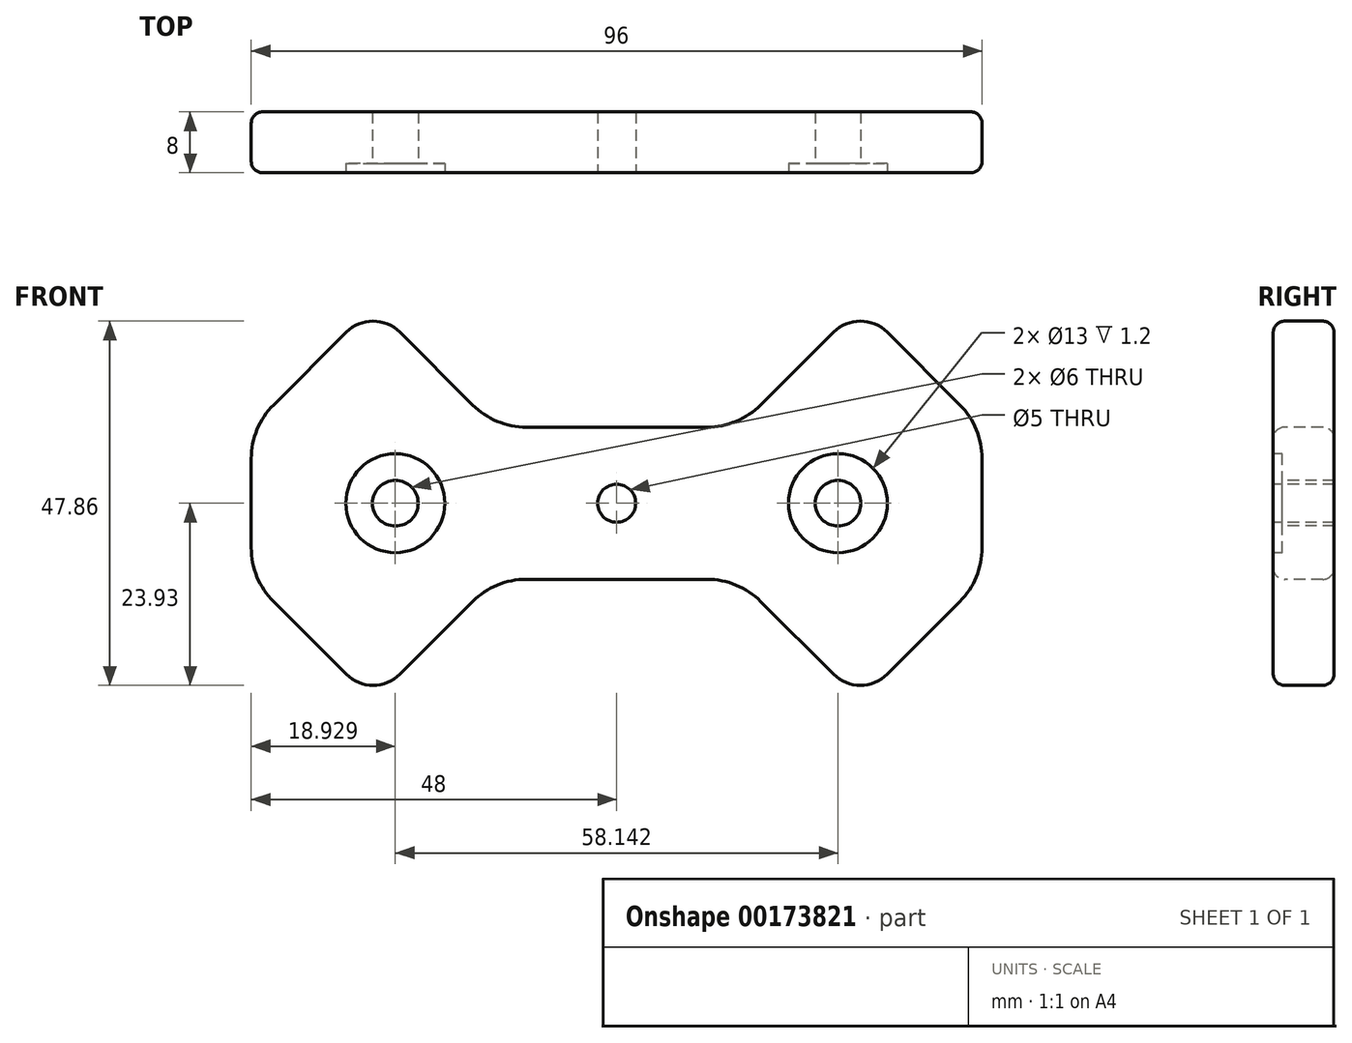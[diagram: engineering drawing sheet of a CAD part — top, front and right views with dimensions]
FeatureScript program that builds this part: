
annotation { "Feature Type Name" : "Feature", "Feature Type Description" : "" }
export const myFeature = defineFeature(function(context is Context, id is Id, definition is map)
    precondition{}
    {
        {
            var Q0;
            Q0=qCreatedBy(makeId("Front.planeOp"),FACE);
            var sketch = newSketch(context, id + "F0", { "sketchPlane" : qUnion([Q0])});
            skLineSegment(sketch, "E0", {"start": v(22, 90.61) * mm, "end": v(22, -125.4) * mm, "construction": true});
            skLineSegment(sketch, "E1", {"start": v(25.54, 3.54) * mm, "end": v(146.18, 124.18) * mm, "construction": true});
            skLineSegment(sketch, "E2", {"start": v(25.54, -3.54) * mm, "end": v(137.79, -115.79) * mm, "construction": true});
            skPoint(sketch, "E3.visualSharp", {"position": v(22, 0) * mm});
            skArc(sketch, "E3.filletArc", {"start": v(25.54, 3.54) * mm, "mid": v(24.07, 0) * mm, "end": v(25.54, -3.54) * mm, "construction": true});
            skLineSegment(sketch, "E4.0", {"start": v(24.2, 4.88) * mm, "end": v(144.83, 125.52) * mm});
            skArc(sketch, "E4.1", {"start": v(24.2, 4.88) * mm, "mid": v(22.17, 0) * mm, "end": v(24.2, -4.88) * mm});
            skLineSegment(sketch, "E4.2", {"start": v(24.2, -4.88) * mm, "end": v(136.44, -117.13) * mm});
            skLineSegment(sketch, "E5.0", {"start": v(26.88, 2.2) * mm, "end": v(147.52, 122.83) * mm});
            skArc(sketch, "E5.1", {"start": v(26.88, 2.2) * mm, "mid": v(25.97, 0) * mm, "end": v(26.88, -2.2) * mm});
            skLineSegment(sketch, "E5.2", {"start": v(26.88, -2.2) * mm, "end": v(139.13, -114.44) * mm});
            skLineSegment(sketch, "E6", {"start": v(0, 0) * mm, "end": v(0, 10) * mm});
            skLineSegment(sketch, "E7", {"start": v(0, 10) * mm, "end": v(11.86, 10) * mm});
            skLineSegment(sketch, "E8", {"start": v(48, 5.86) * mm, "end": v(48, -5.86) * mm});
            skLineSegment(sketch, "E9", {"start": v(0, -10) * mm, "end": v(0, 0) * mm});
            skLineSegment(sketch, "E10", {"start": v(45.07, 12.93) * mm, "end": v(35.54, 22.46) * mm});
            skLineSegment(sketch, "E11", {"start": v(28.46, 22.46) * mm, "end": v(18.93, 12.93) * mm});
            skLineSegment(sketch, "E12", {"start": v(18.93, -12.93) * mm, "end": v(28.46, -22.46) * mm});
            skLineSegment(sketch, "E13", {"start": v(35.54, -22.46) * mm, "end": v(45.07, -12.93) * mm});
            skLineSegment(sketch, "E14.trimOffspring", {"start": v(11.86, -10) * mm, "end": v(0, -10) * mm});
            skCircle(sketch, "E15", {"center": v(29.07, 0) * mm, "radius": 6.5 * mm});
            skPoint(sketch, "E16.visualSharp", {"position": v(16, 10) * mm});
            skArc(sketch, "E16.filletArc", {"start": v(11.86, 10) * mm, "mid": v(15.68, 10.76) * mm, "end": v(18.93, 12.93) * mm});
            skPoint(sketch, "E17.visualSharp", {"position": v(16, -10) * mm});
            skArc(sketch, "E17.filletArc", {"start": v(18.93, -12.93) * mm, "mid": v(15.68, -10.76) * mm, "end": v(11.86, -10) * mm});
            skPoint(sketch, "E18.visualSharp", {"position": v(32, 26) * mm});
            skArc(sketch, "E18.filletArc", {"start": v(35.54, 22.46) * mm, "mid": v(32, 23.93) * mm, "end": v(28.46, 22.46) * mm});
            skPoint(sketch, "E19.visualSharp", {"position": v(32, -26) * mm});
            skArc(sketch, "E19.filletArc", {"start": v(28.46, -22.46) * mm, "mid": v(32, -23.93) * mm, "end": v(35.54, -22.46) * mm});
            skPoint(sketch, "E20.visualSharp", {"position": v(48, 10) * mm});
            skArc(sketch, "E20.filletArc", {"start": v(48, 5.86) * mm, "mid": v(47.24, 9.68) * mm, "end": v(45.07, 12.93) * mm});
            skPoint(sketch, "E21.visualSharp", {"position": v(48, -10) * mm});
            skArc(sketch, "E21.filletArc", {"start": v(45.07, -12.93) * mm, "mid": v(47.24, -9.68) * mm, "end": v(48, -5.86) * mm});
            skSolve(sketch);
        }
        {
            var Q0;
            Q0=qSketchRegion(id+"F0",true);
            var Q1;
            {var subQ0=sQuery(id+"F0.wireOp",EDGE,"E5.1");Q1=makeQuery(id+"F0.imprint","IMPRINT",FACE,{"disambiguationData":[TD([[makeQuery(id+"F0.imprint","IMPRINT",EDGE,{"derivedFrom":subQ0}),1.0]])]});}
            var Q2;
            {var subQ0=sQuery(id+"F0.wireOp",EDGE,"E5.1");Q2=makeQuery(id+"F0.imprint","IMPRINT",FACE,{"disambiguationData":[TD([[makeQuery(id+"F0.imprint","IMPRINT",EDGE,{"derivedFrom":subQ0}),-1.0]])]});}
            extrude(context, id + "F1", {"entities" : qUnion([Q0, Q1, Q2]), "oppositeDirection" : true, "depth" : 8 * mm, "offsetDistance" : 25 * mm});
        }
        {
            var Q0;
            Q0=makeQuery(id+"F1.opExtrude","SWEPT_FACE",FACE,{"disambiguationData":[OSD([sQuery(id+"F0.wireOp",EDGE,"E10")])]});
            var sketch = newSketch(context, id + "F2", { "sketchPlane" : qUnion([Q0])});
            skPoint(sketch, "E22.0", {"position": v(13.66, 0) * mm});
            skPoint(sketch, "E23.0", {"position": v(17.46, 0) * mm});
            skLineSegment(sketch, "E24", {"start": v(17.46, 0) * mm, "end": v(17.46, 1.1) * mm});
            skArc(sketch, "E25", {"start": v(17.46, 1.1) * mm, "mid": v(15.56, 3) * mm, "end": v(13.66, 1.1) * mm});
            skLineSegment(sketch, "E26", {"start": v(17.46, 0) * mm, "end": v(13.66, 0) * mm});
            skLineSegment(sketch, "E27", {"start": v(13.66, 0) * mm, "end": v(13.66, 1.1) * mm});
            skSolve(sketch);
        }
        {
            var Q0;
            Q0=makeQuery(id+"F2.imprint","IMPRINT",FACE,{"disambiguationData":[TD([[makeQuery(id+"F2.imprint","IMPRINT",EDGE,{"derivedFrom":sQuery(id+"F2.wireOp",EDGE,"E24")}),1.0]])]});
            var Q1;
            Q1=sQuery(id+"F0.wireOp",EDGE,"E4.0");
            var Q2;
            Q2=sQuery(id+"F0.wireOp",EDGE,"E4.1");
            var Q3;
            Q3=sQuery(id+"F0.wireOp",EDGE,"E4.2");
            sweep(context, id + "F3", {"operationType" : NewBodyOperationType.REMOVE, "profiles" : qUnion([Q0]), "path" : qUnion([Q1, Q2, Q3])});
        }
        {
            var Q0;
            {var subQ0=sQuery(id+"F0.wireOp",EDGE,"E5.1");Q0=makeQuery(id+"F0.imprint","IMPRINT",FACE,{"disambiguationData":[TD([[makeQuery(id+"F0.imprint","IMPRINT",EDGE,{"derivedFrom":subQ0}),1.0]])]});}
            var sketch = newSketch(context, id + "F4", { "sketchPlane" : qUnion([Q0])});
            skCircle(sketch, "E28.0", {"center": v(29.07, 0) * mm, "radius": 6.5 * mm});
            skSolve(sketch);
        }
        {
            var Q0;
            Q0=qSketchRegion(id+"F4",true);
            extrude(context, id + "F5", {"entities" : qUnion([Q0]), "operationType" : NewBodyOperationType.REMOVE, "oppositeDirection" : true, "depth" : 1.2 * mm, "offsetDistance" : 25 * mm});
        }
        {
            var Q0;
            {var subQ0=sQuery(id+"F0.wireOp",EDGE,"E5.1");Q0=makeQuery(id+"F0.imprint","IMPRINT",FACE,{"disambiguationData":[TD([[makeQuery(id+"F0.imprint","IMPRINT",EDGE,{"derivedFrom":subQ0}),1.0]])]});}
            var sketch = newSketch(context, id + "F6", { "sketchPlane" : qUnion([Q0])});
            skPoint(sketch, "E29.0", {"position": v(29.07, 0) * mm});
            skCircle(sketch, "E30", {"center": v(29.07, 0) * mm, "radius": 3 * mm});
            skSolve(sketch);
        }
        {
            var Q0;
            Q0=qSketchRegion(id+"F6",true);
            extrude(context, id + "F7", {"entities" : qUnion([Q0]), "operationType" : NewBodyOperationType.REMOVE, "oppositeDirection" : true, "depth" : 38 * mm, "offsetDistance" : 25 * mm});
        }
        {
            var Q0;
            Q0=makeQuery(id+"F60TyKU6r4YqE7J_2.opLoft","SWEPT_BODY",BODY,{"disambiguationData":[OSD([sQuery(id+"F0.wireOp",EDGE,"E6"),sQuery(id+"F0.wireOp",EDGE,"E7"),sQuery(id+"F0.wireOp",EDGE,"E8"),sQuery(id+"F0.wireOp",EDGE,"E9"),sQuery(id+"F0.wireOp",EDGE,"E10"),sQuery(id+"F0.wireOp",EDGE,"E11"),sQuery(id+"F0.wireOp",EDGE,"E12"),sQuery(id+"F0.wireOp",EDGE,"E13"),sQuery(id+"F0.wireOp",EDGE,"E14.trimOffspring"),sQuery(id+"F0.wireOp",EDGE,"E16.filletArc"),sQuery(id+"F0.wireOp",EDGE,"E17.filletArc"),sQuery(id+"F0.wireOp",EDGE,"E18.filletArc"),sQuery(id+"F0.wireOp",EDGE,"E19.filletArc"),sQuery(id+"F0.wireOp",EDGE,"E20.filletArc"),sQuery(id+"F0.wireOp",EDGE,"E21.filletArc"),makeQuery(id+"FDdhLqWOSWDpHas_2.imprint","IMPRINT",FACE,{"disambiguationData":[TD([[makeQuery(id+"FDdhLqWOSWDpHas_2.imprint","IMPRINT",EDGE,{"derivedFrom":sQuery(id+"FDdhLqWOSWDpHas_2.wireOp",EDGE,"zI8NPd9Y-P4wq-rvJP-xVdT-J3jt9JK9rZbD.bottom")}),1.0]])]})])]});
            var Q1;
            Q1=makeQuery(id+"F1.opExtrude","SWEPT_BODY",BODY,{"disambiguationData":[OSD([sQuery(id+"F0.wireOp",EDGE,"E6"),sQuery(id+"F0.wireOp",EDGE,"E7"),sQuery(id+"F0.wireOp",EDGE,"E8"),sQuery(id+"F0.wireOp",EDGE,"E9"),sQuery(id+"F0.wireOp",EDGE,"E10"),sQuery(id+"F0.wireOp",EDGE,"E11"),sQuery(id+"F0.wireOp",EDGE,"E12"),sQuery(id+"F0.wireOp",EDGE,"E13"),sQuery(id+"F0.wireOp",EDGE,"E14.trimOffspring"),sQuery(id+"F0.wireOp",EDGE,"E16.filletArc"),sQuery(id+"F0.wireOp",EDGE,"E17.filletArc"),sQuery(id+"F0.wireOp",EDGE,"E18.filletArc"),sQuery(id+"F0.wireOp",EDGE,"E19.filletArc"),sQuery(id+"F0.wireOp",EDGE,"E20.filletArc"),sQuery(id+"F0.wireOp",EDGE,"E21.filletArc")])]});
            var Q2;
            Q2=qCreatedBy(makeId("Right.planeOp"),FACE);
            mirror(context, id + "F8", {"operationType" : NewBodyOperationType.ADD, "entities" : qUnion([Q0, Q1]), "mirrorPlane" : qUnion([Q2])});
        }
        {
            var Q0;
            {var subQ0=sQuery(id+"F0.wireOp",EDGE,"E18.filletArc");var subQ1=sQuery(id+"F0.wireOp",EDGE,"E17.filletArc");var subQ2=sQuery(id+"F0.wireOp",EDGE,"E16.filletArc");var subQ3=sQuery(id+"F0.wireOp",EDGE,"E14.trimOffspring");var subQ4=sQuery(id+"F0.wireOp",EDGE,"E13");var subQ5=sQuery(id+"F0.wireOp",EDGE,"E12");var subQ6=sQuery(id+"F0.wireOp",EDGE,"E9");var subQ7=sQuery(id+"F0.wireOp",EDGE,"E6");var subQ8=sQuery(id+"F0.wireOp",EDGE,"E7");var subQ9=sQuery(id+"F0.wireOp",EDGE,"E10");var subQ10=sQuery(id+"F0.wireOp",EDGE,"E11");var subQ11=sQuery(id+"F0.wireOp",EDGE,"E19.filletArc");var subQ13=makeQuery(id+"F3.boolean.opBoolean","SPLIT",FACE,{"disambiguationData":[TD([makeQuery(id+"F1.opExtrude","SWEPT_FACE",FACE,{"disambiguationData":[OSD([subQ8])]})])],"derivedFrom":makeQuery(id+"F1.opExtrude","CAP_FACE",FACE,{"disambiguationData":[OSD([subQ7,subQ8,sQuery(id+"F0.wireOp",EDGE,"E8"),subQ6,subQ9,subQ10,subQ5,subQ4,subQ3,subQ2,subQ1,subQ0,subQ11,sQuery(id+"F0.wireOp",EDGE,"E20.filletArc"),sQuery(id+"F0.wireOp",EDGE,"E21.filletArc")])],"isStart":true})});Q0=makeQuery(id+"F8.boolean.opBoolean","MERGE",FACE,{"derivedFrom":[subQ13,makeQuery(id+"F8.opPattern","COPY",FACE,{"derivedFrom":subQ13,"instanceName":"1"})]});}
            var sketch = newSketch(context, id + "F9", { "sketchPlane" : qUnion([Q0])});
            skCircle(sketch, "E31", {"center": v(0, 0) * mm, "radius": 2.5 * mm});
            skSolve(sketch);
        }
        {
            var Q0;
            Q0=qSketchRegion(id+"F9",true);
            extrude(context, id + "F10", {"entities" : qUnion([Q0]), "operationType" : NewBodyOperationType.REMOVE, "oppositeDirection" : true, "depth" : 22 * mm, "offsetDistance" : 25 * mm});
        }
        {
            var Q0;
            Q0=makeQuery(id+"F1.opExtrude","CAP_EDGE",EDGE,{"disambiguationData":[OSD([sQuery(id+"F0.wireOp",EDGE,"E21.filletArc")])],"isStart":true});
            var Q1;
            Q1=makeQuery(id+"F1.opExtrude","CAP_EDGE",EDGE,{"disambiguationData":[OSD([sQuery(id+"F0.wireOp",EDGE,"E11")])],"isStart":true});
            var Q2;
            Q2=makeQuery(id+"F8.opPattern","COPY",EDGE,{"derivedFrom":makeQuery(id+"F1.opExtrude","CAP_EDGE",EDGE,{"disambiguationData":[OSD([sQuery(id+"F0.wireOp",EDGE,"E8")])],"isStart":true}),"instanceName":"1"});
            var Q3;
            {var subQ0=makeQuery(id+"F1.opExtrude","CAP_EDGE",EDGE,{"disambiguationData":[OSD([sQuery(id+"F0.wireOp",EDGE,"E14.trimOffspring")])],"isStart":true});Q3=makeQuery(id+"F8.boolean.opBoolean","MERGE",EDGE,{"derivedFrom":[subQ0,makeQuery(id+"F8.opPattern","COPY",EDGE,{"derivedFrom":subQ0,"instanceName":"1"})]});}
            var Q4;
            {var subQ0=makeQuery(id+"F1.opExtrude","CAP_EDGE",EDGE,{"disambiguationData":[OSD([sQuery(id+"F0.wireOp",EDGE,"E14.trimOffspring")])],"isStart":false});Q4=makeQuery(id+"F8.boolean.opBoolean","MERGE",EDGE,{"derivedFrom":[subQ0,makeQuery(id+"F8.opPattern","COPY",EDGE,{"derivedFrom":subQ0,"instanceName":"1"})]});}
            fillet(context, id + "F11", {"entities" : qUnion([Q0, Q1, Q2, Q3, Q4]), "radius" : 1.5 * mm, "tangentPropagation" : true, "allowEdgeOverflow" : false});
        }
    });
